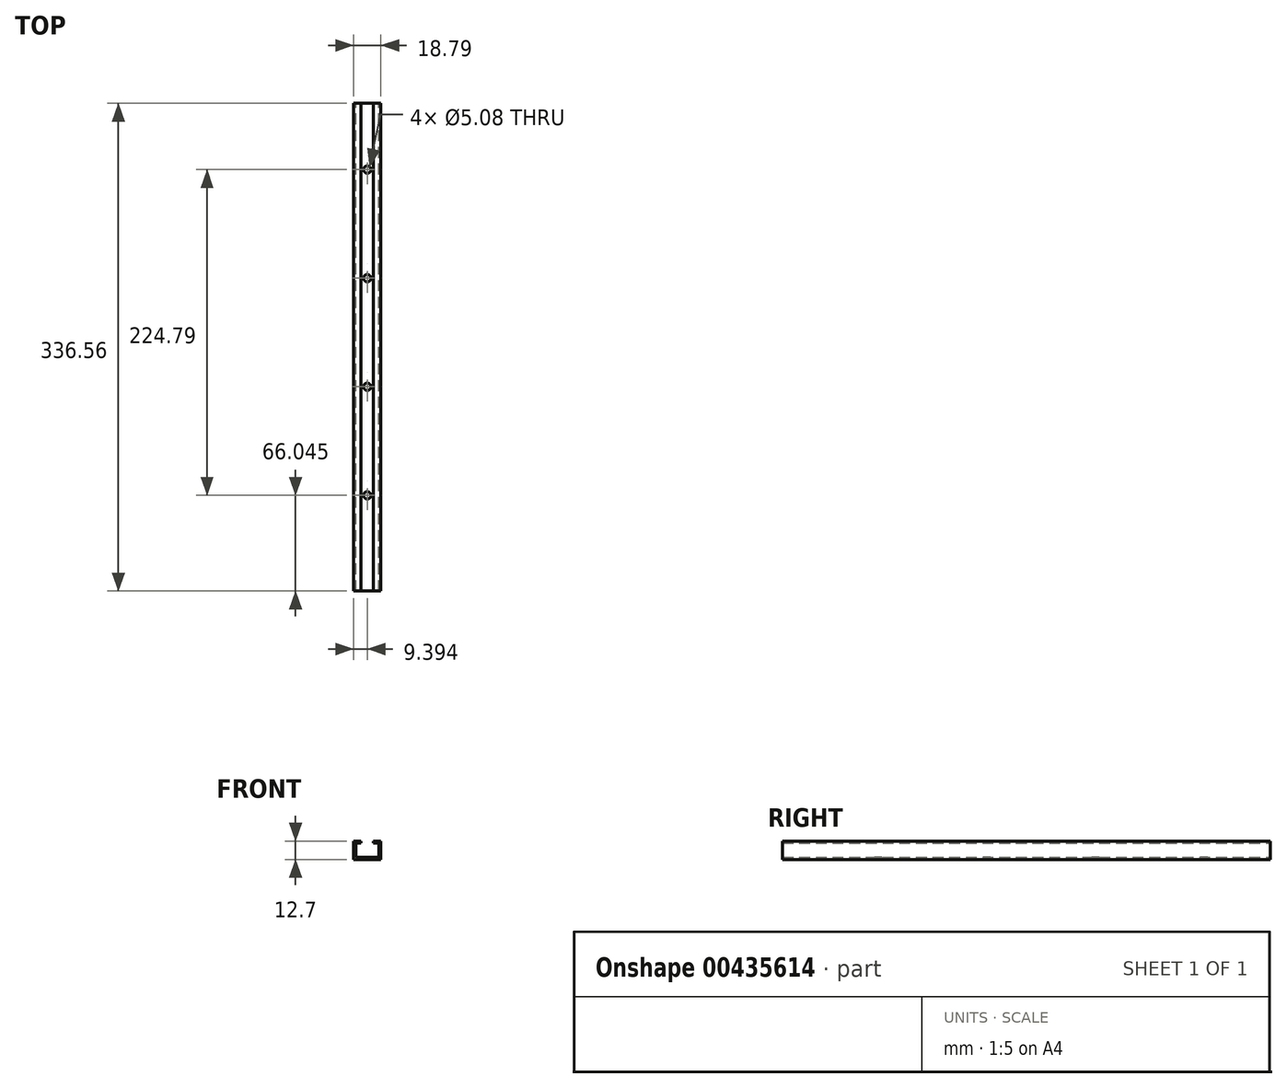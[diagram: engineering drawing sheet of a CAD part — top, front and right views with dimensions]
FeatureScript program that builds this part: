
annotation { "Feature Type Name" : "Feature", "Feature Type Description" : "" }
export const myFeature = defineFeature(function(context is Context, id is Id, definition is map)
    precondition{}
    {
        {
            var Q0;
            Q0=qCreatedBy(makeId("Front.planeOp"),FACE);
            var sketch = newSketch(context, id + "F0", { "sketchPlane" : qUnion([Q0])});
            skLineSegment(sketch, "E0", {"start": v(-27.35, 24.12) * mm, "end": v(-27.35, 26.3) * mm});
            skLineSegment(sketch, "E1", {"start": v(-27.35, 26.3) * mm, "end": v(-32.43, 26.3) * mm});
            skLineSegment(sketch, "E2", {"start": v(-32.43, 26.3) * mm, "end": v(-32.43, 13.6) * mm});
            skLineSegment(sketch, "E3", {"start": v(-32.43, 13.6) * mm, "end": v(-13.64, 13.6) * mm});
            skLineSegment(sketch, "E4", {"start": v(-13.64, 13.6) * mm, "end": v(-13.64, 26.3) * mm});
            skLineSegment(sketch, "E5", {"start": v(-13.64, 26.3) * mm, "end": v(-18.72, 26.3) * mm});
            skLineSegment(sketch, "E6", {"start": v(-18.72, 26.3) * mm, "end": v(-18.72, 24.77) * mm});
            skLineSegment(sketch, "E7", {"start": v(-18.72, 24.77) * mm, "end": v(-15.16, 24.77) * mm});
            skLineSegment(sketch, "E8", {"start": v(-15.16, 24.77) * mm, "end": v(-15.16, 15.12) * mm});
            skLineSegment(sketch, "E9", {"start": v(-15.16, 15.12) * mm, "end": v(-30.91, 15.12) * mm});
            skLineSegment(sketch, "E10", {"start": v(-30.91, 15.12) * mm, "end": v(-30.91, 24.77) * mm});
            skLineSegment(sketch, "E11", {"start": v(-30.91, 24.77) * mm, "end": v(-27.35, 24.77) * mm});
            skSolve(sketch);
        }
        {
            var Q0;
            {var subQ0=sQuery(id+"F0.wireOp",EDGE,"E1");Q0=makeQuery(id+"F0.imprint","IMPRINT",FACE,{"disambiguationData":[TD([[makeQuery(id+"F0.imprint","IMPRINT",EDGE,{"derivedFrom":subQ0}),1.0]])]});}
            extrude(context, id + "F1", {"entities" : qUnion([Q0]), "depth" : 336.55 * mm, "symmetric" : true});
        }
        {
            var Q0;
            Q0=makeQuery(id+"F1.opExtrude","SWEPT_FACE",FACE,{"disambiguationData":[OSD([sQuery(id+"F0.wireOp",EDGE,"E3")])]});
            var sketch = newSketch(context, id + "F2", { "sketchPlane" : qUnion([Q0])});
            skPoint(sketch, "E12", {"position": v(-23.04, 102.23) * mm});
            skPoint(sketch, "E13", {"position": v(-23.04, 27.3) * mm});
            skPoint(sketch, "E14", {"position": v(-23.04, -122.56) * mm});
            skPoint(sketch, "E15", {"position": v(-23.04, -47.63) * mm});
            skSolve(sketch);
        }
        {
            var Q0;
            Q0=sQuery(id+"F2.wireOp",VERTEX,"E12");
            var Q1;
            Q1=sQuery(id+"F2.wireOp",VERTEX,"E13");
            var Q2;
            Q2=sQuery(id+"F2.wireOp",VERTEX,"E15");
            var Q3;
            Q3=sQuery(id+"F2.wireOp",VERTEX,"E14");
            var Q4;
            Q4=makeQuery(id+"F1.opExtrude","SWEPT_BODY",BODY,{"disambiguationData":[OSD([sQuery(id+"F0.wireOp",EDGE,"E0"),sQuery(id+"F0.wireOp",EDGE,"E1"),sQuery(id+"F0.wireOp",EDGE,"E2"),sQuery(id+"F0.wireOp",EDGE,"E3"),sQuery(id+"F0.wireOp",EDGE,"E4"),sQuery(id+"F0.wireOp",EDGE,"E5"),sQuery(id+"F0.wireOp",EDGE,"E6"),sQuery(id+"F0.wireOp",EDGE,"E7"),sQuery(id+"F0.wireOp",EDGE,"E8"),sQuery(id+"F0.wireOp",EDGE,"E9"),sQuery(id+"F0.wireOp",EDGE,"E10"),sQuery(id+"F0.wireOp",EDGE,"E11")])]});
            hole(context, id + "F3", {"style" : HoleStyle.SIMPLE, "endStyle" : HoleEndStyle.BLIND, "holeDiameter" : 5.08 * mm, "holeDepth" : 25.4 * mm, "isTappedThrough" : true, "tappedDepth" : 12.7 * mm, "tapClearance" : 3, "locations" : qUnion([Q0, Q1, Q2, Q3]), "scope" : qUnion([Q4])});
        }
    });
